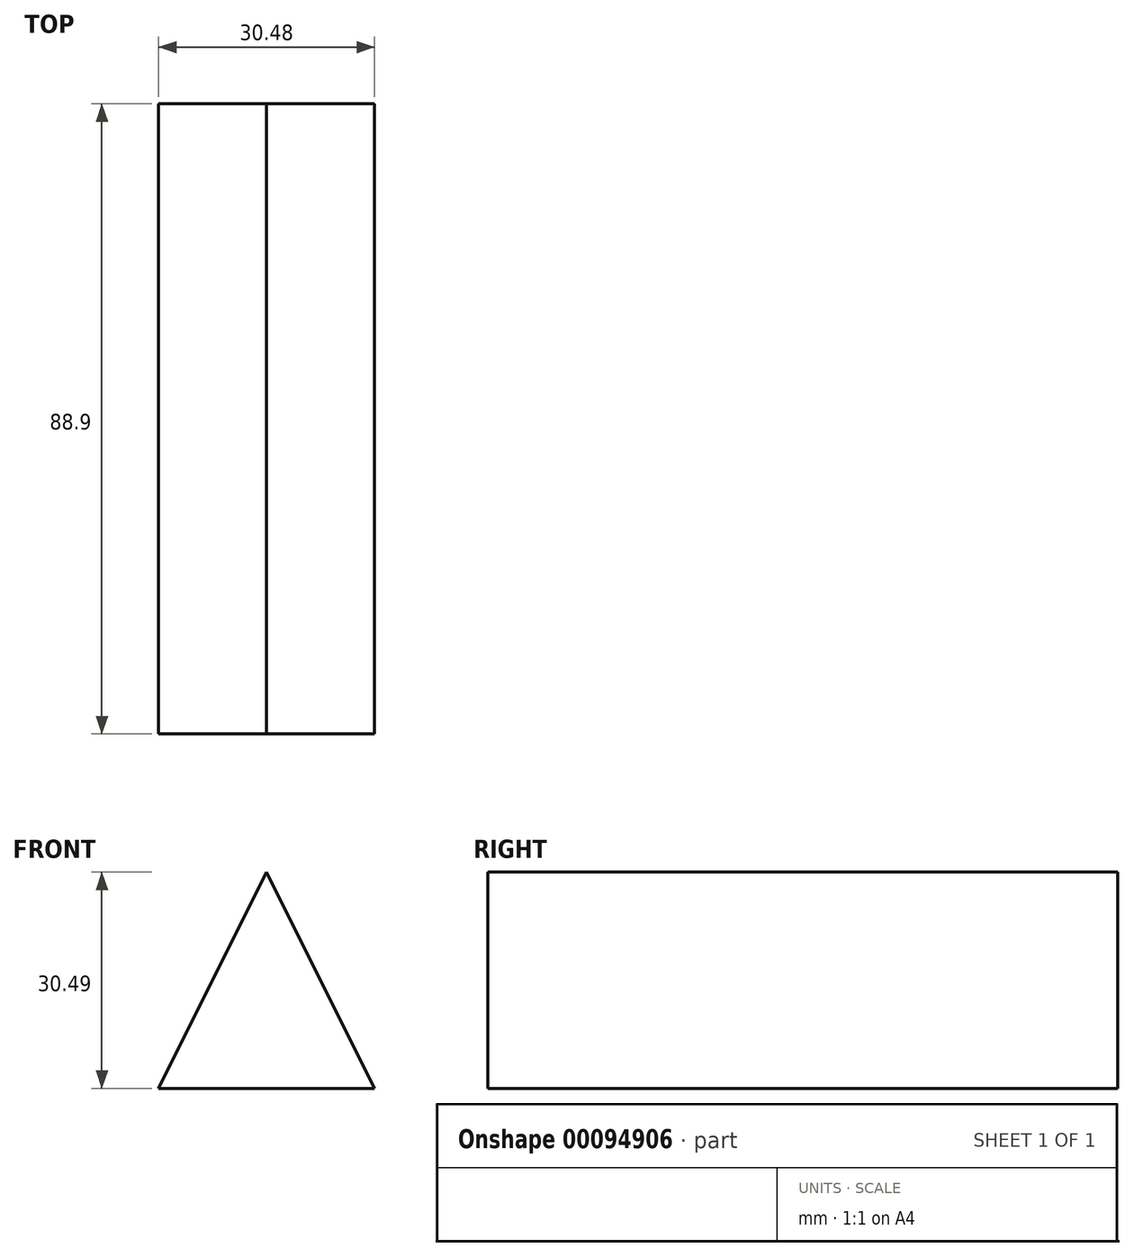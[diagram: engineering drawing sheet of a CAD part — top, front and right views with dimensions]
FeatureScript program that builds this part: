
annotation { "Feature Type Name" : "Feature", "Feature Type Description" : "" }
export const myFeature = defineFeature(function(context is Context, id is Id, definition is map)
    precondition{}
    {
        {
            var Q0;
            Q0=qCreatedBy(makeId("Front.planeOp"),FACE);
            var sketch = newSketch(context, id + "F0", { "sketchPlane" : qUnion([Q0])});
            skLineSegment(sketch, "E0", {"start": v(-48.7, 7.7) * mm, "end": v(-18.23, 7.7) * mm});
            skLineSegment(sketch, "E1", {"start": v(-18.23, 7.7) * mm, "end": v(-33.47, 38.2) * mm});
            skLineSegment(sketch, "E2", {"start": v(-33.47, 38.2) * mm, "end": v(-48.7, 7.7) * mm});
            skSolve(sketch);
        }
        {
            var Q0;
            Q0 = qSketchRegion(id + "F0", true);
            extrude(context, id + "F1", {"entities" : qUnion([Q0]), "depth" : 88.9 * mm});
        }
    });
